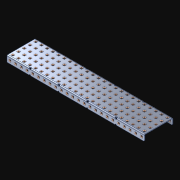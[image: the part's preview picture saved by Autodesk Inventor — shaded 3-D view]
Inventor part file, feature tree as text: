
AUTODESK INVENTOR PART (.ipt)
format: ipt  version: 2021 (Build 250183000, 183)  size: 2,124,800 bytes
history: native  units: in
note: dims shown in document units (in); Inventor stores cm internally (conversion verified against a paired STEP export)
features: extrude x169, other x169, sketch x4, pattern_linear x3
ambient origin geometry x8: Origin, YZ Plane, XZ Plane, XY Plane, X Axis, Y Axis, Z Axis, Center Point
bodies: Solid1 (feature_tree)
feature tree (345):
  pattern_linear  "Rectangular Pattern1"  Spacing1=0.182in  [1 undecoded]
  pattern_linear  "Rectangular Pattern2"  Spacing1=0.046in  [1 undecoded]
  pattern_linear  "Rectangular Pattern3"  Spacing1=0.5in  [1 undecoded]
  extrude  "Extrusion1"  Depth=0.046in
  sketch  "Sketch1"  dims[d0=0.182in]
  other  "Srf1"
  sketch  "Sketch2"  dims[d1=0.046in d2=0.0in]
  other  "Srf2"
  sketch  "Sketch3"  dims[d3=0.182in]
  other  "Srf3"
  other  "Srf4"
  other  "Srf5"
  other  "Srf6"
  other  "Srf7"
  other  "Srf8"
  other  "Srf9"
  other  "Srf10"
  other  "Srf11"
  other  "Srf12"
  other  "Srf13"
  other  "Srf14"
  other  "Srf15"
  other  "Srf16"
  other  "Srf17"
  other  "Srf18"
  other  "Srf19"
  other  "Srf20"
  other  "Srf21"
  other  "Srf22"
  other  "Srf23"
  other  "Srf24"
  other  "Srf25"
  other  "Srf26"
  other  "Srf38"
  other  "Srf39"
  other  "Srf40"
  other  "Srf41"
  other  "Srf42"
  other  "Srf43"
  other  "Srf44"
  other  "Srf45"
  other  "Srf46"
  other  "Srf47"
  other  "Srf48"
  other  "Srf49"
  other  "Srf50"
  other  "Srf51"
  other  "Srf52"
  other  "Srf53"
  other  "Srf54"
  other  "Srf55"
  other  "Srf56"
  other  "Srf57"
  other  "Srf58"
  other  "Srf59"
  other  "Srf60"
  other  "Srf72"
  other  "Srf73"
  other  "Srf74"
  other  "Srf75"
  other  "Srf76"
  other  "Srf77"
  other  "Srf78"
  other  "Srf79"
  other  "Srf80"
  other  "Srf81"
  other  "Srf82"
  other  "Srf83"
  other  "Srf84"
  other  "Srf85"
  other  "Srf86"
  other  "Srf87"
  other  "Srf88"
  other  "Srf89"
  other  "Srf90"
  other  "Srf91"
  other  "Srf92"
  other  "Srf93"
  other  "Srf94"
  other  "Srf95"
  other  "Srf107"
  other  "Srf108"
  other  "Srf109"
  other  "Srf110"
  other  "Srf111"
  other  "Srf112"
  other  "Srf113"
  other  "Srf114"
  other  "Srf115"
  other  "Srf116"
  other  "Srf117"
  other  "Srf118"
  other  "Srf119"
  other  "Srf120"
  other  "Srf121"
  other  "Srf122"
  other  "Srf123"
  other  "Srf124"
  other  "Srf125"
  other  "Srf126"
  other  "Srf127"
  other  "Srf128"
  other  "Srf129"
  other  "Srf130"
  other  "Srf142"
  other  "Srf143"
  other  "Srf144"
  other  "Srf145"
  other  "Srf146"
  other  "Srf147"
  other  "Srf148"
  other  "Srf149"
  other  "Srf150"
  other  "Srf151"
  other  "Srf152"
  other  "Srf153"
  other  "Srf154"
  other  "Srf155"
  other  "Srf156"
  other  "Srf157"
  other  "Srf158"
  other  "Srf159"
  other  "Srf160"
  other  "Srf161"
  other  "Srf162"
  other  "Srf163"
  other  "Srf164"
  other  "Srf165"
  other  "Srf177"
  other  "Srf178"
  other  "Srf179"
  other  "Srf180"
  other  "Srf181"
  other  "Srf182"
  other  "Srf183"
  other  "Srf184"
  other  "Srf185"
  other  "Srf186"
  other  "Srf187"
  other  "Srf188"
  other  "Srf189"
  other  "Srf190"
  other  "Srf191"
  other  "Srf192"
  other  "Srf193"
  other  "Srf194"
  other  "Srf195"
  other  "Srf196"
  other  "Srf197"
  other  "Srf198"
  other  "Srf199"
  other  "Srf200"
  other  "Srf212"
  other  "Srf213"
  other  "Srf214"
  other  "Srf215"
  other  "Srf216"
  other  "Srf217"
  other  "Srf218"
  other  "Srf219"
  other  "Srf220"
  other  "Srf221"
  other  "Srf222"
  other  "Srf223"
  other  "Srf224"
  other  "Srf225"
  other  "Srf226"
  other  "Srf227"
  other  "Srf228"
  other  "Srf229"
  other  "Srf230"
  other  "Srf231"
  other  "Srf232"
  other  "Srf233"
  other  "Srf234"
  sketch  "Sketch4"  dims[d4=0.046in d5=0.0in d6=0.182in d7=0.046in d8=0.0in d11=0.5in d12=9.4488in d14=0.5in d15=1.9685in d17=0.5in d18=9.4488in d20=0.5in d21=5.5in d22=0.0in]
  parser-record x1  (decoder bookkeeping rows leaked as tree rows — omitted from the tree; the rows remain in map.json)
  extrude  "ExtrusionSrf1"  Depth=0.046in
  extrude  "ExtrusionSrf2"  Depth=0.046in
  extrude  "ExtrusionSrf3"  Depth=0.046in
  extrude  "ExtrusionSrf4"  Depth=0.046in
  extrude  "ExtrusionSrf5"  Depth=0.046in
  extrude  "ExtrusionSrf6"  TaperAngle=0.0deg  [1 undecoded]
  extrude  "ExtrusionSrf7"  [1 undecoded]
  extrude  "ExtrusionSrf8"  [1 undecoded]
  extrude  "ExtrusionSrf9"  [1 undecoded]
  extrude  "ExtrusionSrf10"  [1 undecoded]
  extrude  "ExtrusionSrf11"  [1 undecoded]
  extrude  "ExtrusionSrf12"  [1 undecoded]
  extrude  "ExtrusionSrf13"  [1 undecoded]
  extrude  "ExtrusionSrf14"  [1 undecoded]
  extrude  "ExtrusionSrf15"  [1 undecoded]
  extrude  "ExtrusionSrf16"  [1 undecoded]
  extrude  "ExtrusionSrf17"  [1 undecoded]
  extrude  "ExtrusionSrf18"  [1 undecoded]
  extrude  "ExtrusionSrf19"  [1 undecoded]
  extrude  "ExtrusionSrf20"  [1 undecoded]
  extrude  "ExtrusionSrf21"  [1 undecoded]
  extrude  "ExtrusionSrf22"  [1 undecoded]
  extrude  "ExtrusionSrf23"  [1 undecoded]
  extrude  "ExtrusionSrf24"  [1 undecoded]
  extrude  "ExtrusionSrf25"  [1 undecoded]
  extrude  "ExtrusionSrf26"  [1 undecoded]
  extrude  "ExtrusionSrf38"  [1 undecoded]
  extrude  "ExtrusionSrf39"  [1 undecoded]
  extrude  "ExtrusionSrf40"  [1 undecoded]
  extrude  "ExtrusionSrf41"  [1 undecoded]
  extrude  "ExtrusionSrf42"  [1 undecoded]
  extrude  "ExtrusionSrf43"  [1 undecoded]
  extrude  "ExtrusionSrf44"  [1 undecoded]
  extrude  "ExtrusionSrf45"  [1 undecoded]
  extrude  "ExtrusionSrf46"  [1 undecoded]
  extrude  "ExtrusionSrf47"  [1 undecoded]
  extrude  "ExtrusionSrf48"  [1 undecoded]
  extrude  "ExtrusionSrf49"  [1 undecoded]
  extrude  "ExtrusionSrf50"  [1 undecoded]
  extrude  "ExtrusionSrf51"  [1 undecoded]
  extrude  "ExtrusionSrf52"  [1 undecoded]
  extrude  "ExtrusionSrf53"  [1 undecoded]
  extrude  "ExtrusionSrf54"  [1 undecoded]
  extrude  "ExtrusionSrf55"  [1 undecoded]
  extrude  "ExtrusionSrf56"  [1 undecoded]
  extrude  "ExtrusionSrf57"  [1 undecoded]
  extrude  "ExtrusionSrf58"  [1 undecoded]
  extrude  "ExtrusionSrf59"  [1 undecoded]
  extrude  "ExtrusionSrf60"  [1 undecoded]
  extrude  "ExtrusionSrf72"  [1 undecoded]
  extrude  "ExtrusionSrf73"  [1 undecoded]
  extrude  "ExtrusionSrf74"  [1 undecoded]
  extrude  "ExtrusionSrf75"  [1 undecoded]
  extrude  "ExtrusionSrf76"  [1 undecoded]
  extrude  "ExtrusionSrf77"  [1 undecoded]
  extrude  "ExtrusionSrf78"  [1 undecoded]
  extrude  "ExtrusionSrf79"  [1 undecoded]
  extrude  "ExtrusionSrf80"  [1 undecoded]
  extrude  "ExtrusionSrf81"  [1 undecoded]
  extrude  "ExtrusionSrf82"  [1 undecoded]
  extrude  "ExtrusionSrf83"  [1 undecoded]
  extrude  "ExtrusionSrf84"  [1 undecoded]
  extrude  "ExtrusionSrf85"  [1 undecoded]
  extrude  "ExtrusionSrf86"  [1 undecoded]
  extrude  "ExtrusionSrf87"  [1 undecoded]
  extrude  "ExtrusionSrf88"  [1 undecoded]
  extrude  "ExtrusionSrf89"  [1 undecoded]
  extrude  "ExtrusionSrf90"  [1 undecoded]
  extrude  "ExtrusionSrf91"  [1 undecoded]
  extrude  "ExtrusionSrf92"  [1 undecoded]
  extrude  "ExtrusionSrf93"  [1 undecoded]
  extrude  "ExtrusionSrf94"  [1 undecoded]
  extrude  "ExtrusionSrf95"  [1 undecoded]
  extrude  "ExtrusionSrf107"  [1 undecoded]
  extrude  "ExtrusionSrf108"  [1 undecoded]
  extrude  "ExtrusionSrf109"  [1 undecoded]
  extrude  "ExtrusionSrf110"  [1 undecoded]
  extrude  "ExtrusionSrf111"  [1 undecoded]
  extrude  "ExtrusionSrf112"  [1 undecoded]
  extrude  "ExtrusionSrf113"  [1 undecoded]
  extrude  "ExtrusionSrf114"  [1 undecoded]
  extrude  "ExtrusionSrf115"  [1 undecoded]
  extrude  "ExtrusionSrf116"  [1 undecoded]
  extrude  "ExtrusionSrf117"  [1 undecoded]
  extrude  "ExtrusionSrf118"  [1 undecoded]
  extrude  "ExtrusionSrf119"  [1 undecoded]
  extrude  "ExtrusionSrf120"  [1 undecoded]
  extrude  "ExtrusionSrf121"  [1 undecoded]
  extrude  "ExtrusionSrf122"  [1 undecoded]
  extrude  "ExtrusionSrf123"  [1 undecoded]
  extrude  "ExtrusionSrf124"  [1 undecoded]
  extrude  "ExtrusionSrf125"  [1 undecoded]
  extrude  "ExtrusionSrf126"  [1 undecoded]
  extrude  "ExtrusionSrf127"  [1 undecoded]
  extrude  "ExtrusionSrf128"  [1 undecoded]
  extrude  "ExtrusionSrf129"  [1 undecoded]
  extrude  "ExtrusionSrf130"  [1 undecoded]
  extrude  "ExtrusionSrf142"  [1 undecoded]
  extrude  "ExtrusionSrf143"  [1 undecoded]
  extrude  "ExtrusionSrf144"  [1 undecoded]
  extrude  "ExtrusionSrf145"  [1 undecoded]
  extrude  "ExtrusionSrf146"  [1 undecoded]
  extrude  "ExtrusionSrf147"  [1 undecoded]
  extrude  "ExtrusionSrf148"  [1 undecoded]
  extrude  "ExtrusionSrf149"  [1 undecoded]
  extrude  "ExtrusionSrf150"  [1 undecoded]
  extrude  "ExtrusionSrf151"  [1 undecoded]
  extrude  "ExtrusionSrf152"  [1 undecoded]
  extrude  "ExtrusionSrf153"  [1 undecoded]
  extrude  "ExtrusionSrf154"  [1 undecoded]
  extrude  "ExtrusionSrf155"  [1 undecoded]
  extrude  "ExtrusionSrf156"  [1 undecoded]
  extrude  "ExtrusionSrf157"  [1 undecoded]
  extrude  "ExtrusionSrf158"  [1 undecoded]
  extrude  "ExtrusionSrf159"  [1 undecoded]
  extrude  "ExtrusionSrf160"  [1 undecoded]
  extrude  "ExtrusionSrf161"  [1 undecoded]
  extrude  "ExtrusionSrf162"  [1 undecoded]
  extrude  "ExtrusionSrf163"  [1 undecoded]
  extrude  "ExtrusionSrf164"  [1 undecoded]
  extrude  "ExtrusionSrf165"  [1 undecoded]
  extrude  "ExtrusionSrf177"  [1 undecoded]
  extrude  "ExtrusionSrf178"  [1 undecoded]
  extrude  "ExtrusionSrf179"  [1 undecoded]
  extrude  "ExtrusionSrf180"  [1 undecoded]
  extrude  "ExtrusionSrf181"  [1 undecoded]
  extrude  "ExtrusionSrf182"  [1 undecoded]
  extrude  "ExtrusionSrf183"  [1 undecoded]
  extrude  "ExtrusionSrf184"  [1 undecoded]
  extrude  "ExtrusionSrf185"  [1 undecoded]
  extrude  "ExtrusionSrf186"  [1 undecoded]
  extrude  "ExtrusionSrf187"  [1 undecoded]
  extrude  "ExtrusionSrf188"  [1 undecoded]
  extrude  "ExtrusionSrf189"  [1 undecoded]
  extrude  "ExtrusionSrf190"  [1 undecoded]
  extrude  "ExtrusionSrf191"  [1 undecoded]
  extrude  "ExtrusionSrf192"  [1 undecoded]
  extrude  "ExtrusionSrf193"  [1 undecoded]
  extrude  "ExtrusionSrf194"  [1 undecoded]
  extrude  "ExtrusionSrf195"  [1 undecoded]
  extrude  "ExtrusionSrf196"  [1 undecoded]
  extrude  "ExtrusionSrf197"  [1 undecoded]
  extrude  "ExtrusionSrf198"  [1 undecoded]
  extrude  "ExtrusionSrf199"  [1 undecoded]
  extrude  "ExtrusionSrf200"  [1 undecoded]
  extrude  "ExtrusionSrf212"  [1 undecoded]
  extrude  "ExtrusionSrf213"  [1 undecoded]
  extrude  "ExtrusionSrf214"  [1 undecoded]
  extrude  "ExtrusionSrf215"  [1 undecoded]
  extrude  "ExtrusionSrf216"  [1 undecoded]
  extrude  "ExtrusionSrf217"  [1 undecoded]
  extrude  "ExtrusionSrf218"  [1 undecoded]
  extrude  "ExtrusionSrf219"  [1 undecoded]
  extrude  "ExtrusionSrf220"  [1 undecoded]
  extrude  "ExtrusionSrf221"  [1 undecoded]
  extrude  "ExtrusionSrf222"  [1 undecoded]
  extrude  "ExtrusionSrf223"  [1 undecoded]
  extrude  "ExtrusionSrf224"  [1 undecoded]
  extrude  "ExtrusionSrf225"  [1 undecoded]
  extrude  "ExtrusionSrf226"  [1 undecoded]
  extrude  "ExtrusionSrf227"  [1 undecoded]
  extrude  "ExtrusionSrf228"  [1 undecoded]
  extrude  "ExtrusionSrf229"  [1 undecoded]
  extrude  "ExtrusionSrf230"  [1 undecoded]
  extrude  "ExtrusionSrf231"  [1 undecoded]
  extrude  "ExtrusionSrf232"  [1 undecoded]
  extrude  "ExtrusionSrf233"  [1 undecoded]
  extrude  "ExtrusionSrf234"  [1 undecoded]
note: 166 required parameter values undecoded (feature->parameter linkage not recoverable at this tier; creation-order binding heuristic only, values carry confidence <= 0.55)
